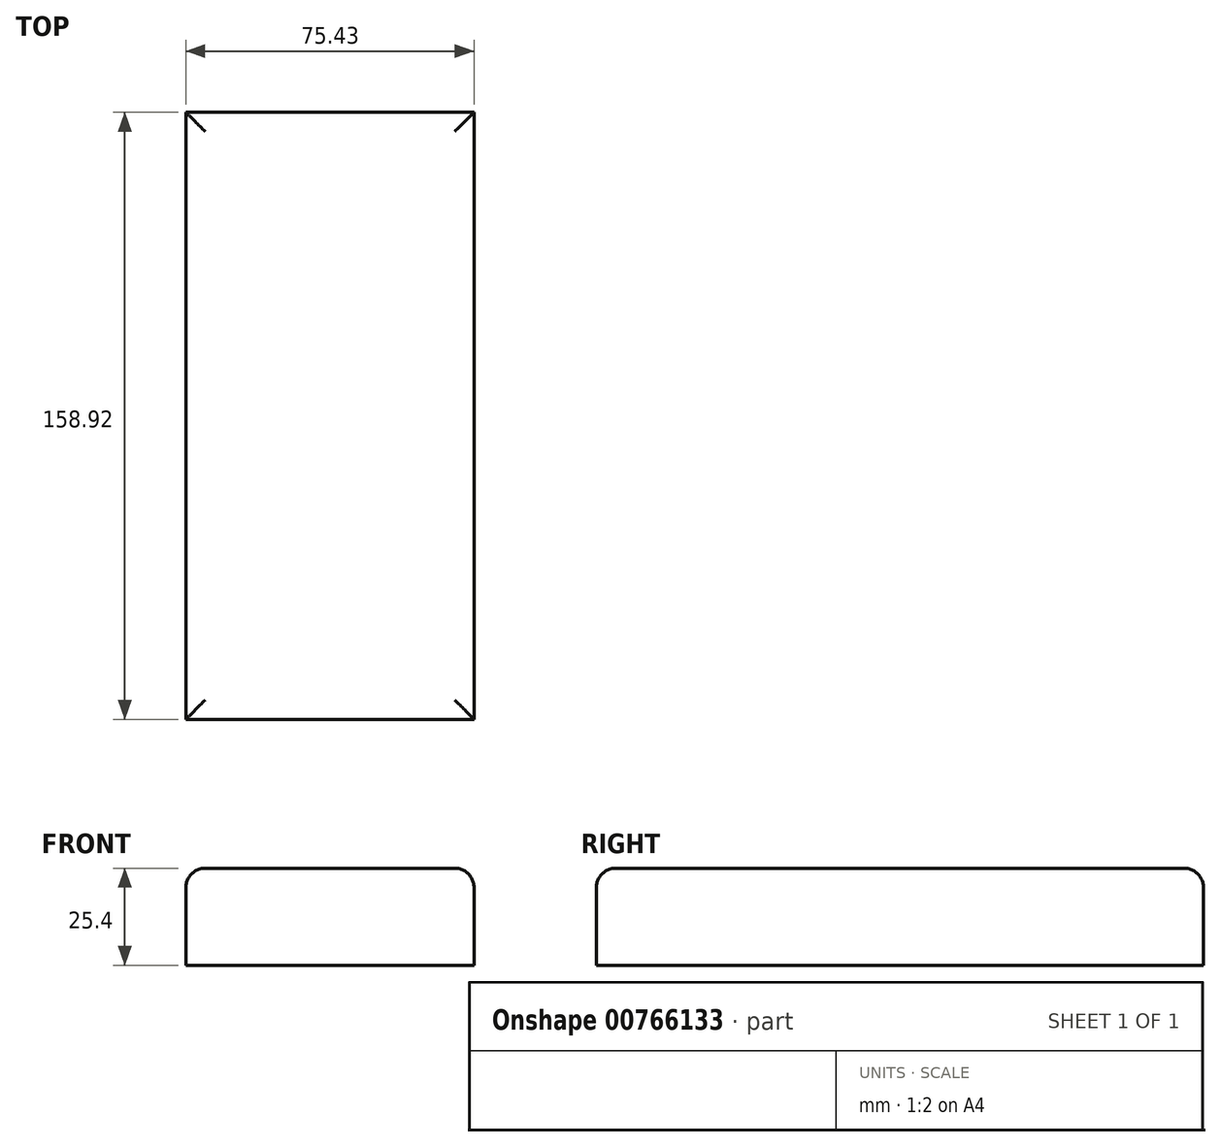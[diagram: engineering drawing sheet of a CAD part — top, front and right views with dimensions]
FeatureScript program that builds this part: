
annotation { "Feature Type Name" : "Feature", "Feature Type Description" : "" }
export const myFeature = defineFeature(function(context is Context, id is Id, definition is map)
    precondition{}
    {
        {
            var Q0;
            Q0=qCreatedBy(makeId("Top.planeOp"),FACE);
            var sketch = newSketch(context, id + "F0", { "sketchPlane" : qUnion([Q0])});
            skLineSegment(sketch, "E0.bottom", {"start": v(0, 0) * mm, "end": v(-76.2, 0) * mm});
            skLineSegment(sketch, "E0.top", {"start": v(0, 76.2) * mm, "end": v(-76.2, 76.2) * mm});
            skLineSegment(sketch, "E0.left", {"start": v(0, 0) * mm, "end": v(0, 76.2) * mm});
            skLineSegment(sketch, "E0.right", {"start": v(-76.2, 0) * mm, "end": v(-76.2, 76.2) * mm});
            skSolve(sketch);
        }
        {
            var Q0;
            Q0=makeQuery(id+"F0.imprint","IMPRINT",FACE,{"disambiguationData":[TD([[makeQuery(id+"F0.imprint","IMPRINT",EDGE,{"derivedFrom":sQuery(id+"F0.wireOp",EDGE,"E0.bottom")}),-1.0]])]});
            extrude(context, id + "F1", {"entities" : qUnion([Q0]), "depth" : 76.2 * mm, "offsetDistance" : 25.4 * mm});
        }
        {
            var Q0;
            Q0=makeQuery(id+"F1.opExtrude","CAP_EDGE",EDGE,{"disambiguationData":[OSD([sQuery(id+"F0.wireOp",EDGE,"E0.bottom")])],"isStart":false});
            var Q1;
            Q1=makeQuery(id+"F1.opExtrude","SWEPT_FACE",FACE,{"disambiguationData":[OSD([sQuery(id+"F0.wireOp",EDGE,"E0.left")])]});
            var Q2;
            Q2=makeQuery(id+"F1.opExtrude","CAP_FACE",FACE,{"disambiguationData":[OSD([sQuery(id+"F0.wireOp",EDGE,"E0.bottom"),sQuery(id+"F0.wireOp",EDGE,"E0.top"),sQuery(id+"F0.wireOp",EDGE,"E0.left"),sQuery(id+"F0.wireOp",EDGE,"E0.right")])],"isStart":false});
            var Q3;
            Q3=makeQuery(id+"F1.opExtrude","CAP_EDGE",EDGE,{"disambiguationData":[OSD([sQuery(id+"F0.wireOp",EDGE,"E0.right")])],"isStart":false});
            var Q4;
            Q4=makeQuery(id+"F1.opExtrude","SWEPT_EDGE",EDGE,{"disambiguationData":[OSD([sQuery(id+"F0.wireOp",EDGE,"E0.bottom"),sQuery(id+"F0.wireOp",EDGE,"E0.right")])]});
            fillet(context, id + "F2", {"entities" : qUnion([Q0, Q1, Q2, Q3, Q4]), "radius" : 5.08 * mm, "tangentPropagation" : true, "allowEdgeOverflow" : false});
        }
        {
            var Q0;
            Q0=makeQuery(id+"F1.opExtrude","SWEPT_BODY",BODY,{"disambiguationData":[OSD([sQuery(id+"F0.wireOp",EDGE,"E0.bottom"),sQuery(id+"F0.wireOp",EDGE,"E0.top"),sQuery(id+"F0.wireOp",EDGE,"E0.left"),sQuery(id+"F0.wireOp",EDGE,"E0.right")])]});
            deleteBodies(context, id + "F3", {"entities" : qUnion([Q0])});
        }
        {
            var Q0;
            Q0=qCreatedBy(makeId("Top.planeOp"),FACE);
            var sketch = newSketch(context, id + "F4", { "sketchPlane" : qUnion([Q0])});
            skLineSegment(sketch, "E1.bottom", {"start": v(0, 0) * mm, "end": v(-76.2, 0) * mm});
            skLineSegment(sketch, "E1.top", {"start": v(0, 76.2) * mm, "end": v(-76.2, 76.2) * mm});
            skLineSegment(sketch, "E1.left", {"start": v(0, 0) * mm, "end": v(0, 76.2) * mm});
            skLineSegment(sketch, "E1.right", {"start": v(-76.2, 0) * mm, "end": v(-76.2, 76.2) * mm});
            skSolve(sketch);
        }
        {
            var Q0;
            Q0 = qSketchRegion(id + "F4", true);
            extrude(context, id + "F5", {"entities" : qUnion([Q0]), "depth" : 76.2 * mm, "offsetDistance" : 25.4 * mm});
        }
        {
            var Q0;
            Q0=makeQuery(id+"F5.opExtrude","SWEPT_FACE",FACE,{"disambiguationData":[OSD([sQuery(id+"F4.wireOp",EDGE,"E1.left")])]});
            var sketch = newSketch(context, id + "F6", { "sketchPlane" : qUnion([Q0])});
            skLineSegment(sketch, "E2.bottom", {"start": v(21.3, 0) * mm, "end": v(72.1, 0) * mm});
            skLineSegment(sketch, "E2.top", {"start": v(21.3, 50.8) * mm, "end": v(72.1, 50.8) * mm});
            skLineSegment(sketch, "E2.left", {"start": v(21.3, 0) * mm, "end": v(21.3, 50.8) * mm});
            skLineSegment(sketch, "E2.right", {"start": v(72.1, 0) * mm, "end": v(72.1, 50.8) * mm});
            skSolve(sketch);
        }
        {
            var Q0;
            Q0 = qSketchRegion(id + "F6", true);
            extrude(context, id + "F7", {"entities" : qUnion([Q0]), "operationType" : NewBodyOperationType.ADD, "depth" : 50.8 * mm, "offsetDistance" : 25.4 * mm});
        }
        {
            var Q0;
            Q0=makeQuery(id+"F5.opExtrude","SWEPT_BODY",BODY,{"disambiguationData":[OSD([sQuery(id+"F4.wireOp",EDGE,"E1.bottom"),sQuery(id+"F4.wireOp",EDGE,"E1.top"),sQuery(id+"F4.wireOp",EDGE,"E1.left"),sQuery(id+"F4.wireOp",EDGE,"E1.right")])]});
            deleteBodies(context, id + "F8", {"entities" : qUnion([Q0])});
        }
        {
            var Q0;
            Q0=qCreatedBy(makeId("Top.planeOp"),FACE);
            var sketch = newSketch(context, id + "F9", { "sketchPlane" : qUnion([Q0])});
            skLineSegment(sketch, "E3.bottom", {"start": v(0, 0) * mm, "end": v(75.43, 0) * mm});
            skLineSegment(sketch, "E3.top", {"start": v(0, 158.92) * mm, "end": v(75.43, 158.92) * mm});
            skLineSegment(sketch, "E3.left", {"start": v(0, 0) * mm, "end": v(0, 158.92) * mm});
            skLineSegment(sketch, "E3.right", {"start": v(75.43, 0) * mm, "end": v(75.43, 158.92) * mm});
            skSolve(sketch);
        }
        {
            var Q0;
            Q0=makeQuery(id+"F9.imprint","IMPRINT",FACE,{"disambiguationData":[TD([[makeQuery(id+"F9.imprint","IMPRINT",EDGE,{"derivedFrom":sQuery(id+"F9.wireOp",EDGE,"E3.bottom")}),1.0]])]});
            extrude(context, id + "F10", {"entities" : qUnion([Q0]), "depth" : 25.4 * mm, "offsetDistance" : 25.4 * mm});
        }
        {
            var Q0;
            Q0=makeQuery(id+"F10.opExtrude","CAP_EDGE",EDGE,{"disambiguationData":[OSD([sQuery(id+"F9.wireOp",EDGE,"E3.bottom")])],"isStart":false});
            var Q1;
            Q1=makeQuery(id+"F10.opExtrude","CAP_EDGE",EDGE,{"disambiguationData":[OSD([sQuery(id+"F9.wireOp",EDGE,"E3.right")])],"isStart":false});
            var Q2;
            Q2=makeQuery(id+"F10.opExtrude","CAP_EDGE",EDGE,{"disambiguationData":[OSD([sQuery(id+"F9.wireOp",EDGE,"E3.top")])],"isStart":false});
            var Q3;
            Q3=makeQuery(id+"F10.opExtrude","CAP_EDGE",EDGE,{"disambiguationData":[OSD([sQuery(id+"F9.wireOp",EDGE,"E3.left")])],"isStart":false});
            fillet(context, id + "F11", {"entities" : qUnion([Q0, Q1, Q2, Q3]), "radius" : 5.08 * mm, "tangentPropagation" : true, "allowEdgeOverflow" : false});
        }
    });
